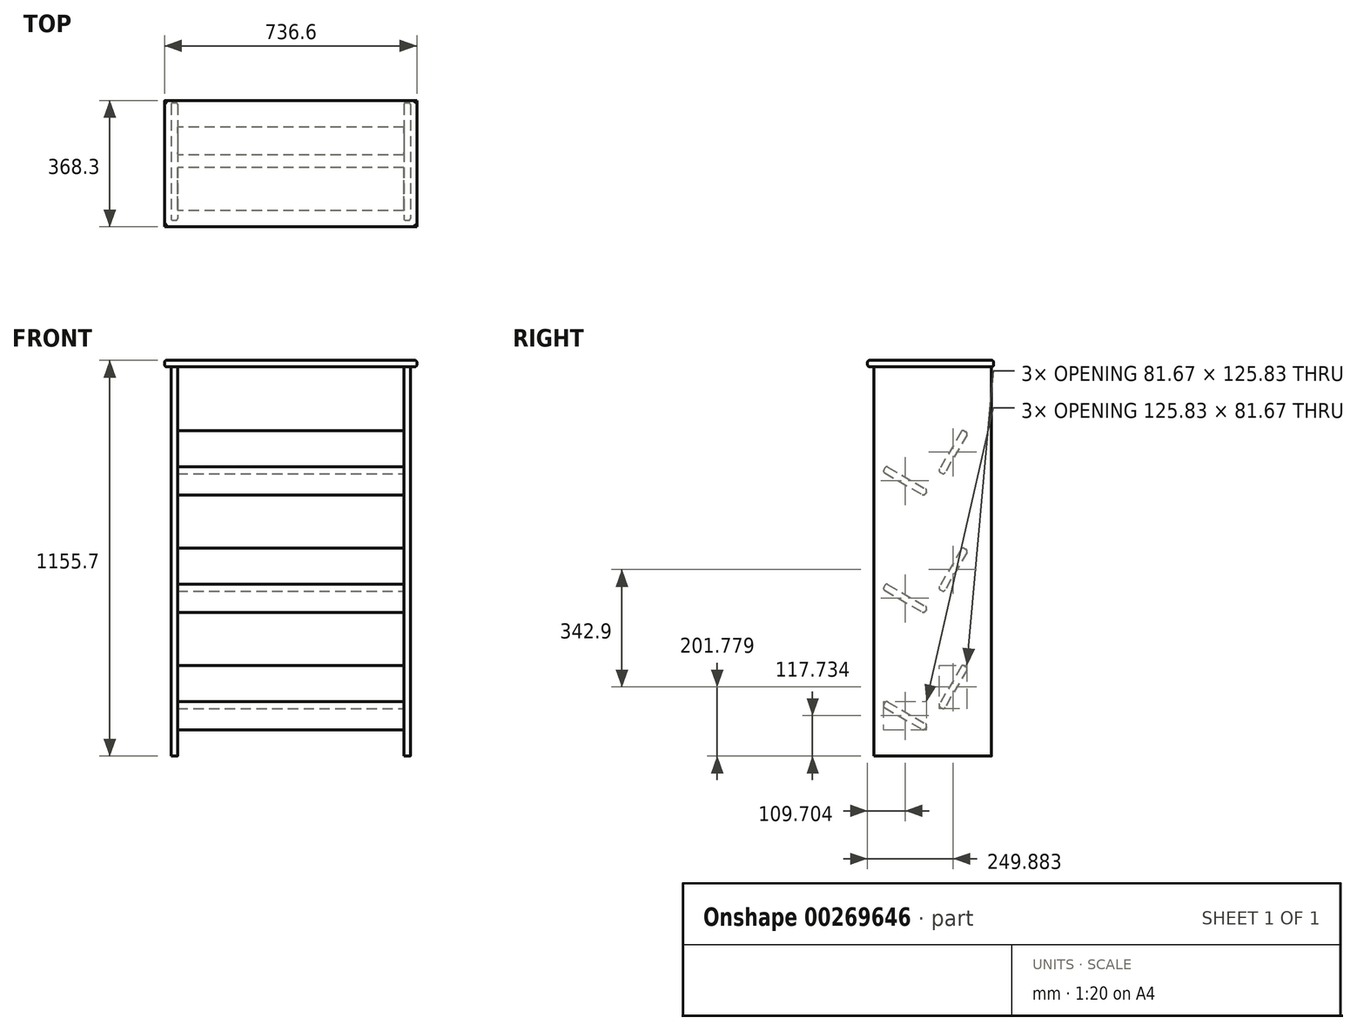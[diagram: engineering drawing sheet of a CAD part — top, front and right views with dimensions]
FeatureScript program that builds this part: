
annotation { "Feature Type Name" : "Feature", "Feature Type Description" : "" }
export const myFeature = defineFeature(function(context is Context, id is Id, definition is map)
    precondition{}
    {
        {
            var Q0;
            Q0=qCreatedBy(makeId("Top.planeOp"),FACE);
            var sketch = newSketch(context, id + "F0", { "sketchPlane" : qUnion([Q0])});
            skLineSegment(sketch, "E0.bottom", {"start": v(0, 0) * mm, "end": v(736.6, 0) * mm});
            skLineSegment(sketch, "E0.top", {"start": v(0, 368.3) * mm, "end": v(736.6, 368.3) * mm});
            skLineSegment(sketch, "E0.left", {"start": v(0, 0) * mm, "end": v(0, 368.3) * mm});
            skLineSegment(sketch, "E0.right", {"start": v(736.6, 0) * mm, "end": v(736.6, 368.3) * mm});
            skSolve(sketch);
        }
        {
            var Q0;
            Q0=qCreatedBy(makeId("Top.planeOp"),FACE);
            var sketch = newSketch(context, id + "F1", { "sketchPlane" : qUnion([Q0])});
            skLineSegment(sketch, "E1.bottom", {"start": v(19.05, 361.95) * mm, "end": v(38.1, 361.95) * mm});
            skLineSegment(sketch, "E1.top", {"start": v(19.05, 19.05) * mm, "end": v(38.1, 19.05) * mm});
            skLineSegment(sketch, "E1.left", {"start": v(19.05, 361.95) * mm, "end": v(19.05, 19.05) * mm});
            skLineSegment(sketch, "E1.right", {"start": v(38.1, 361.95) * mm, "end": v(38.1, 19.05) * mm});
            skLineSegment(sketch, "E2.bottom", {"start": v(698.5, 361.95) * mm, "end": v(717.55, 361.95) * mm});
            skLineSegment(sketch, "E2.top", {"start": v(698.5, 19.05) * mm, "end": v(717.55, 19.05) * mm});
            skLineSegment(sketch, "E2.left", {"start": v(698.5, 361.95) * mm, "end": v(698.5, 19.05) * mm});
            skLineSegment(sketch, "E2.right", {"start": v(717.55, 361.95) * mm, "end": v(717.55, 19.05) * mm});
            skSolve(sketch);
        }
        {
            var Q0;
            Q0 = qSketchRegion(id + "F0", true);
            extrude(context, id + "F2", {"entities" : qUnion([Q0]), "depth" : 19.05 * mm});
        }
        {
            var Q0;
            Q0=makeQuery(id+"F2.opExtrude","CAP_FACE",FACE,{"disambiguationData":[OSD([sQuery(id+"F0.wireOp",EDGE,"E0.bottom"),sQuery(id+"F0.wireOp",EDGE,"E0.top"),sQuery(id+"F0.wireOp",EDGE,"E0.left"),sQuery(id+"F0.wireOp",EDGE,"E0.right")])],"isStart":false});
            var Q1;
            Q1=makeQuery(id+"F2.opExtrude","CAP_FACE",FACE,{"disambiguationData":[OSD([sQuery(id+"F0.wireOp",EDGE,"E0.bottom"),sQuery(id+"F0.wireOp",EDGE,"E0.top"),sQuery(id+"F0.wireOp",EDGE,"E0.left"),sQuery(id+"F0.wireOp",EDGE,"E0.right")])],"isStart":true});
            fillet(context, id + "F3", {"entities" : qUnion([Q0, Q1]), "radius" : 6.35 * mm, "tangentPropagation" : true, "allowEdgeOverflow" : false});
        }
        {
            var Q0;
            Q0 = qSketchRegion(id + "F1", true);
            extrude(context, id + "F4", {"entities" : qUnion([Q0]), "operationType" : NewBodyOperationType.ADD, "oppositeDirection" : true, "depth" : 1136.65 * mm});
        }
        {
            var Q0;
            Q0=makeQuery(id+"F4.opExtrude","SWEPT_EDGE",EDGE,{"disambiguationData":[OSD([sQuery(id+"F1.wireOp",EDGE,"E1.top"),sQuery(id+"F1.wireOp",EDGE,"E1.right")])]});
            var Q1;
            Q1=makeQuery(id+"F4.opExtrude","SWEPT_EDGE",EDGE,{"disambiguationData":[OSD([sQuery(id+"F1.wireOp",EDGE,"E1.bottom"),sQuery(id+"F1.wireOp",EDGE,"E1.right")])]});
            var Q2;
            Q2=makeQuery(id+"F4.opExtrude","SWEPT_EDGE",EDGE,{"disambiguationData":[OSD([sQuery(id+"F1.wireOp",EDGE,"E1.bottom"),sQuery(id+"F1.wireOp",EDGE,"E1.left")])]});
            var Q3;
            Q3=makeQuery(id+"F4.opExtrude","SWEPT_EDGE",EDGE,{"disambiguationData":[OSD([sQuery(id+"F1.wireOp",EDGE,"E1.top"),sQuery(id+"F1.wireOp",EDGE,"E1.left")])]});
            var Q4;
            Q4=makeQuery(id+"F4.opExtrude","SWEPT_EDGE",EDGE,{"disambiguationData":[OSD([sQuery(id+"F1.wireOp",EDGE,"E2.bottom"),sQuery(id+"F1.wireOp",EDGE,"E2.left")])]});
            var Q5;
            Q5=makeQuery(id+"F4.opExtrude","SWEPT_EDGE",EDGE,{"disambiguationData":[OSD([sQuery(id+"F1.wireOp",EDGE,"E2.top"),sQuery(id+"F1.wireOp",EDGE,"E2.left")])]});
            var Q6;
            Q6=makeQuery(id+"F4.opExtrude","SWEPT_EDGE",EDGE,{"disambiguationData":[OSD([sQuery(id+"F1.wireOp",EDGE,"E2.top"),sQuery(id+"F1.wireOp",EDGE,"E2.right")])]});
            var Q7;
            Q7=makeQuery(id+"F4.opExtrude","SWEPT_EDGE",EDGE,{"disambiguationData":[OSD([sQuery(id+"F1.wireOp",EDGE,"E2.bottom"),sQuery(id+"F1.wireOp",EDGE,"E2.right")])]});
            fillet(context, id + "F5", {"entities" : qUnion([Q0, Q1, Q2, Q3, Q4, Q5, Q6, Q7]), "radius" : 5.08 * mm, "allowEdgeOverflow" : false});
        }
        {
            var Q0;
            Q0=makeQuery(id+"F4.opExtrude","SWEPT_FACE",FACE,{"disambiguationData":[OSD([sQuery(id+"F1.wireOp",EDGE,"E1.right")])]});
            var sketch = newSketch(context, id + "F6", { "sketchPlane" : qUnion([Q0])});
            skLineSegment(sketch, "E3.bottom", {"start": v(53.97, -289.94) * mm, "end": v(174.96, -359.8) * mm});
            skLineSegment(sketch, "E3.top", {"start": v(44.45, -306.44) * mm, "end": v(165.43, -376.3) * mm});
            skLineSegment(sketch, "E3.left", {"start": v(53.97, -289.94) * mm, "end": v(44.45, -306.44) * mm});
            skLineSegment(sketch, "E3.right", {"start": v(174.96, -359.8) * mm, "end": v(165.43, -376.3) * mm});
            skLineSegment(sketch, "E4.bottom", {"start": v(276.56, -183.82) * mm, "end": v(293.06, -193.34) * mm});
            skLineSegment(sketch, "E4.top", {"start": v(206.7, -304.8) * mm, "end": v(223.2, -314.32) * mm});
            skLineSegment(sketch, "E4.left", {"start": v(276.56, -183.82) * mm, "end": v(206.7, -304.8) * mm});
            skLineSegment(sketch, "E4.right", {"start": v(293.06, -193.34) * mm, "end": v(223.2, -314.32) * mm});
            skLineSegment(sketch, "E5", {"start": v(165.43, -376.3) * mm, "end": v(24.13, -376.3) * mm, "construction": true});
            skLineSegment(sketch, "E6.bottom", {"start": v(53.97, -632.84) * mm, "end": v(174.96, -702.7) * mm});
            skLineSegment(sketch, "E6.top", {"start": v(44.45, -649.34) * mm, "end": v(165.43, -719.2) * mm});
            skLineSegment(sketch, "E6.left", {"start": v(53.97, -632.84) * mm, "end": v(44.45, -649.34) * mm});
            skLineSegment(sketch, "E6.right", {"start": v(174.96, -702.7) * mm, "end": v(165.43, -719.2) * mm});
            skLineSegment(sketch, "E7.bottom", {"start": v(276.56, -526.72) * mm, "end": v(293.06, -536.24) * mm});
            skLineSegment(sketch, "E7.top", {"start": v(206.7, -647.7) * mm, "end": v(223.2, -657.22) * mm});
            skLineSegment(sketch, "E7.left", {"start": v(276.56, -526.72) * mm, "end": v(206.7, -647.7) * mm});
            skLineSegment(sketch, "E7.right", {"start": v(293.06, -536.24) * mm, "end": v(223.2, -657.22) * mm});
            skLineSegment(sketch, "E8", {"start": v(165.43, -719.2) * mm, "end": v(24.13, -719.2) * mm, "construction": true});
            skLineSegment(sketch, "E9.bottom", {"start": v(53.97, -975.74) * mm, "end": v(174.96, -1045.6) * mm});
            skLineSegment(sketch, "E9.top", {"start": v(44.45, -992.24) * mm, "end": v(165.43, -1062.1) * mm});
            skLineSegment(sketch, "E9.left", {"start": v(53.97, -975.74) * mm, "end": v(44.45, -992.24) * mm});
            skLineSegment(sketch, "E9.right", {"start": v(174.96, -1045.6) * mm, "end": v(165.43, -1062.1) * mm});
            skLineSegment(sketch, "E10.bottom", {"start": v(276.56, -869.62) * mm, "end": v(293.06, -879.14) * mm});
            skLineSegment(sketch, "E10.top", {"start": v(206.7, -990.6) * mm, "end": v(223.2, -1000.12) * mm});
            skLineSegment(sketch, "E10.left", {"start": v(276.56, -869.62) * mm, "end": v(206.7, -990.6) * mm});
            skLineSegment(sketch, "E10.right", {"start": v(293.06, -879.14) * mm, "end": v(223.2, -1000.12) * mm});
            skLineSegment(sketch, "E11", {"start": v(165.43, -1062.1) * mm, "end": v(24.13, -1062.1) * mm, "construction": true});
            skSolve(sketch);
        }
        {
            var Q0;
            Q0 = qSketchRegion(id + "F6", true);
            extrude(context, id + "F7", {"entities" : qUnion([Q0]), "operationType" : NewBodyOperationType.ADD, "depth" : 660.4 * mm});
        }
        {
            var Q0;
            Q0=makeQuery(id+"F7.opExtrude","SWEPT_EDGE",EDGE,{"disambiguationData":[OSD([sQuery(id+"F6.wireOp",EDGE,"E4.bottom"),sQuery(id+"F6.wireOp",EDGE,"E4.left")])]});
            var Q1;
            Q1=makeQuery(id+"F7.opExtrude","SWEPT_EDGE",EDGE,{"disambiguationData":[OSD([sQuery(id+"F6.wireOp",EDGE,"E4.top"),sQuery(id+"F6.wireOp",EDGE,"E4.left")])]});
            var Q2;
            Q2=makeQuery(id+"F7.opExtrude","SWEPT_EDGE",EDGE,{"disambiguationData":[OSD([sQuery(id+"F6.wireOp",EDGE,"E3.bottom"),sQuery(id+"F6.wireOp",EDGE,"E3.left")])]});
            var Q3;
            Q3=makeQuery(id+"F7.opExtrude","SWEPT_EDGE",EDGE,{"disambiguationData":[OSD([sQuery(id+"F6.wireOp",EDGE,"E3.top"),sQuery(id+"F6.wireOp",EDGE,"E3.left")])]});
            var Q4;
            Q4=makeQuery(id+"F7.opExtrude","SWEPT_EDGE",EDGE,{"disambiguationData":[OSD([sQuery(id+"F6.wireOp",EDGE,"E7.bottom"),sQuery(id+"F6.wireOp",EDGE,"E7.left")])]});
            var Q5;
            Q5=makeQuery(id+"F7.opExtrude","SWEPT_EDGE",EDGE,{"disambiguationData":[OSD([sQuery(id+"F6.wireOp",EDGE,"E7.top"),sQuery(id+"F6.wireOp",EDGE,"E7.left")])]});
            var Q6;
            Q6=makeQuery(id+"F7.opExtrude","SWEPT_EDGE",EDGE,{"disambiguationData":[OSD([sQuery(id+"F6.wireOp",EDGE,"E6.bottom"),sQuery(id+"F6.wireOp",EDGE,"E6.left")])]});
            var Q7;
            Q7=makeQuery(id+"F7.opExtrude","SWEPT_EDGE",EDGE,{"disambiguationData":[OSD([sQuery(id+"F6.wireOp",EDGE,"E6.top"),sQuery(id+"F6.wireOp",EDGE,"E6.left")])]});
            var Q8;
            Q8=makeQuery(id+"F7.opExtrude","SWEPT_EDGE",EDGE,{"disambiguationData":[OSD([sQuery(id+"F6.wireOp",EDGE,"E10.bottom"),sQuery(id+"F6.wireOp",EDGE,"E10.left")])]});
            var Q9;
            Q9=makeQuery(id+"F7.opExtrude","SWEPT_EDGE",EDGE,{"disambiguationData":[OSD([sQuery(id+"F6.wireOp",EDGE,"E10.top"),sQuery(id+"F6.wireOp",EDGE,"E10.left")])]});
            var Q10;
            Q10=makeQuery(id+"F7.opExtrude","SWEPT_EDGE",EDGE,{"disambiguationData":[OSD([sQuery(id+"F6.wireOp",EDGE,"E9.bottom"),sQuery(id+"F6.wireOp",EDGE,"E9.left")])]});
            var Q11;
            Q11=makeQuery(id+"F7.opExtrude","SWEPT_EDGE",EDGE,{"disambiguationData":[OSD([sQuery(id+"F6.wireOp",EDGE,"E9.top"),sQuery(id+"F6.wireOp",EDGE,"E9.left")])]});
            var Q12;
            Q12=makeQuery(id+"F7.opExtrude","SWEPT_EDGE",EDGE,{"disambiguationData":[OSD([sQuery(id+"F6.wireOp",EDGE,"E9.top"),sQuery(id+"F6.wireOp",EDGE,"E9.right")])]});
            var Q13;
            Q13=makeQuery(id+"F7.opExtrude","SWEPT_EDGE",EDGE,{"disambiguationData":[OSD([sQuery(id+"F6.wireOp",EDGE,"E9.bottom"),sQuery(id+"F6.wireOp",EDGE,"E9.right")])]});
            var Q14;
            Q14=makeQuery(id+"F7.opExtrude","SWEPT_EDGE",EDGE,{"disambiguationData":[OSD([sQuery(id+"F6.wireOp",EDGE,"E10.top"),sQuery(id+"F6.wireOp",EDGE,"E10.right")])]});
            var Q15;
            Q15=makeQuery(id+"F7.opExtrude","SWEPT_EDGE",EDGE,{"disambiguationData":[OSD([sQuery(id+"F6.wireOp",EDGE,"E10.bottom"),sQuery(id+"F6.wireOp",EDGE,"E10.right")])]});
            var Q16;
            Q16=makeQuery(id+"F7.opExtrude","SWEPT_EDGE",EDGE,{"disambiguationData":[OSD([sQuery(id+"F6.wireOp",EDGE,"E6.top"),sQuery(id+"F6.wireOp",EDGE,"E6.right")])]});
            var Q17;
            Q17=makeQuery(id+"F7.opExtrude","SWEPT_EDGE",EDGE,{"disambiguationData":[OSD([sQuery(id+"F6.wireOp",EDGE,"E6.bottom"),sQuery(id+"F6.wireOp",EDGE,"E6.right")])]});
            var Q18;
            Q18=makeQuery(id+"F7.opExtrude","SWEPT_EDGE",EDGE,{"disambiguationData":[OSD([sQuery(id+"F6.wireOp",EDGE,"E7.top"),sQuery(id+"F6.wireOp",EDGE,"E7.right")])]});
            var Q19;
            Q19=makeQuery(id+"F7.opExtrude","SWEPT_EDGE",EDGE,{"disambiguationData":[OSD([sQuery(id+"F6.wireOp",EDGE,"E7.bottom"),sQuery(id+"F6.wireOp",EDGE,"E7.right")])]});
            var Q20;
            Q20=makeQuery(id+"F7.opExtrude","SWEPT_EDGE",EDGE,{"disambiguationData":[OSD([sQuery(id+"F6.wireOp",EDGE,"E3.top"),sQuery(id+"F6.wireOp",EDGE,"E3.right")])]});
            var Q21;
            Q21=makeQuery(id+"F7.opExtrude","SWEPT_EDGE",EDGE,{"disambiguationData":[OSD([sQuery(id+"F6.wireOp",EDGE,"E3.bottom"),sQuery(id+"F6.wireOp",EDGE,"E3.right")])]});
            var Q22;
            Q22=makeQuery(id+"F7.opExtrude","SWEPT_EDGE",EDGE,{"disambiguationData":[OSD([sQuery(id+"F6.wireOp",EDGE,"E4.top"),sQuery(id+"F6.wireOp",EDGE,"E4.right")])]});
            var Q23;
            Q23=makeQuery(id+"F7.opExtrude","SWEPT_EDGE",EDGE,{"disambiguationData":[OSD([sQuery(id+"F6.wireOp",EDGE,"E4.bottom"),sQuery(id+"F6.wireOp",EDGE,"E4.right")])]});
            fillet(context, id + "F8", {"entities" : qUnion([Q0, Q1, Q2, Q3, Q4, Q5, Q6, Q7, Q8, Q9, Q10, Q11, Q12, Q13, Q14, Q15, Q16, Q17, Q18, Q19, Q20, Q21, Q22, Q23]), "radius" : 6.35 * mm, "tangentPropagation" : true, "allowEdgeOverflow" : false});
        }
    });
